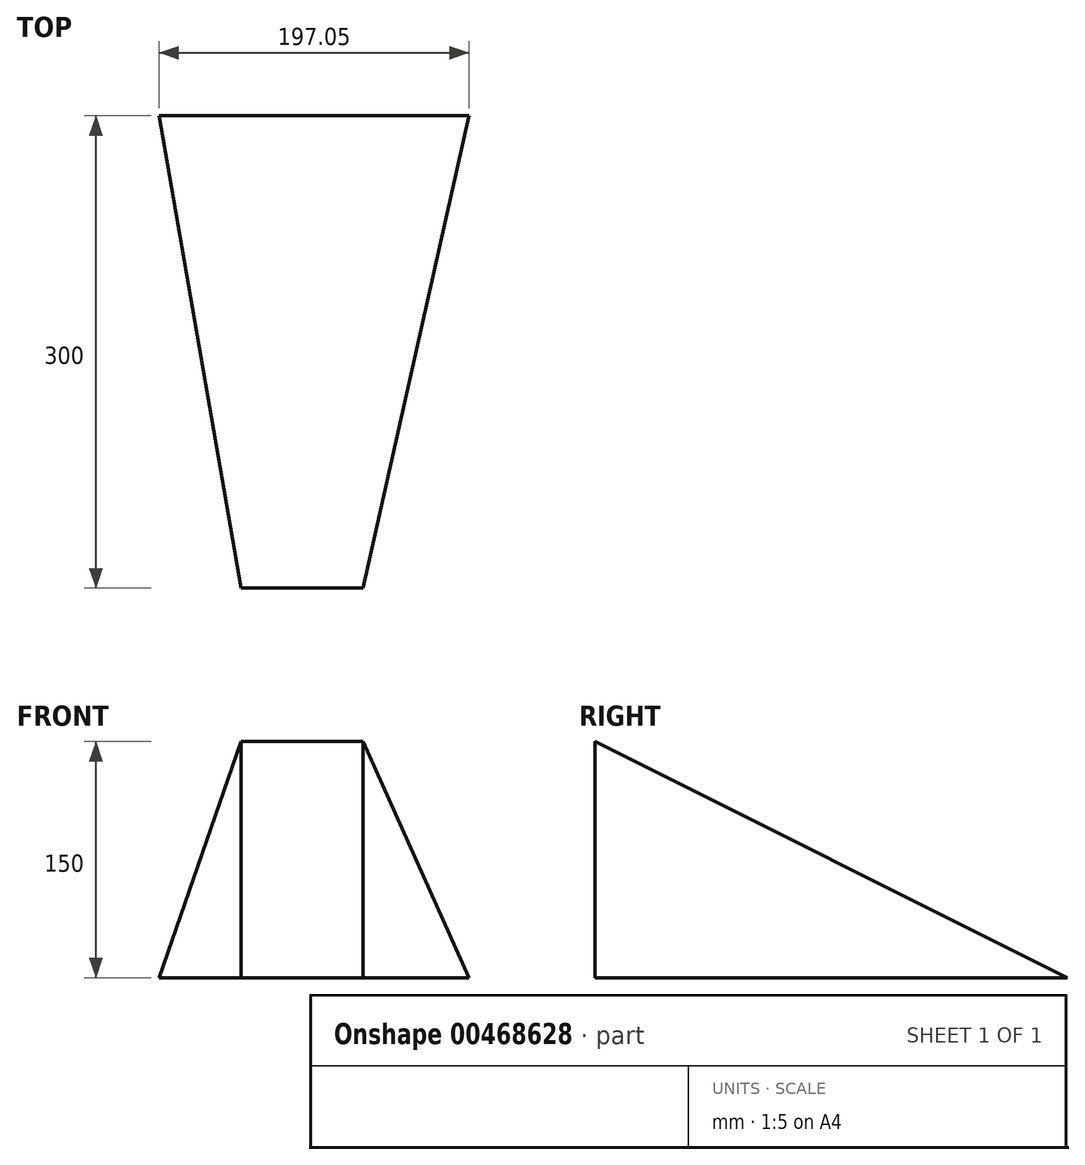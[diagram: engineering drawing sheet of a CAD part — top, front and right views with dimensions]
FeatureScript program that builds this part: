
annotation { "Feature Type Name" : "Feature", "Feature Type Description" : "" }
export const myFeature = defineFeature(function(context is Context, id is Id, definition is map)
    precondition{}
    {
        {
            var Q0;
            Q0=qCreatedBy(makeId("Top.planeOp"),FACE);
            var sketch = newSketch(context, id + "F0", { "sketchPlane" : qUnion([Q0]) });
            skLineSegment(sketch, "E0.bottom", {"start": v(-52.06, 300) * mm, "end": v(0, 0) * mm});
            skLineSegment(sketch, "E1", {"start": v(77.63, 0) * mm, "end": v(145, 300) * mm});
            skLineSegment(sketch, "E2", {"start": v(77.63, 0) * mm, "end": v(0, 0) * mm});
            skLineSegment(sketch, "E3", {"start": v(145, 300) * mm, "end": v(-52.06, 300) * mm});
            skSolve(sketch);
        }
        {
            var Q0;
            Q0=makeQuery(id+"F0.imprint","IMPRINT",FACE,{"disambiguationData":[TD([[makeQuery(id+"F0.imprint","IMPRINT",EDGE,{"derivedFrom":sQuery(id+"F0.wireOp",EDGE,"E0.bottom")}),1.0]])]});
            extrude(context, id + "F1", {"entities" : qUnion([Q0]), "depth" : 150 * mm, "offsetDistance" : 25 * mm});
        }
        {
            var Q0;
            Q0=qCreatedBy(makeId("Right.planeOp"),FACE);
            var sketch = newSketch(context, id + "F2", { "sketchPlane" : qUnion([Q0]) });
            skLineSegment(sketch, "E4", {"start": v(300, 0) * mm, "end": v(0, 150) * mm});
            skLineSegment(sketch, "E5", {"start": v(0, 150) * mm, "end": v(300, 150) * mm});
            skLineSegment(sketch, "E6", {"start": v(300, 150) * mm, "end": v(300, 0) * mm});
            skSolve(sketch);
        }
        {
            var Q0;
            Q0 = qSketchRegion(id + "F2", true);
            extrude(context, id + "F3", {"entities" : qUnion([Q0]), "operationType" : NewBodyOperationType.REMOVE, "endBound" : BoundingType.SYMMETRIC, "depth" : 1000 * mm, "offsetDistance" : 25 * mm});
        }
    });
